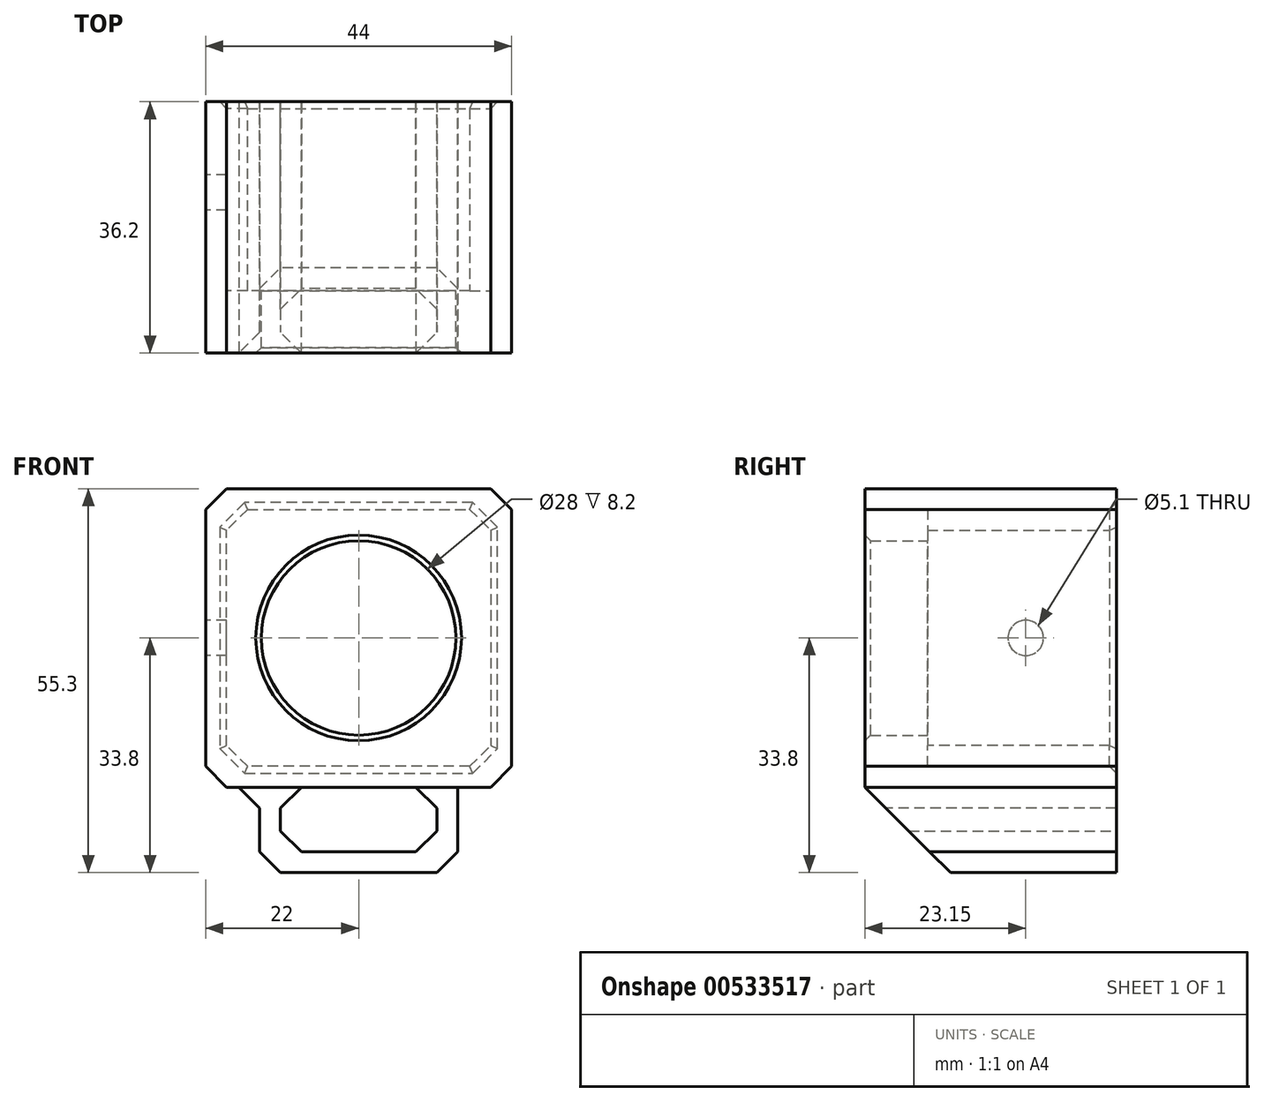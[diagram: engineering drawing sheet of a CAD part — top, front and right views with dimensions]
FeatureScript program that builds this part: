
annotation { "Feature Type Name" : "Feature", "Feature Type Description" : "" }
export const myFeature = defineFeature(function(context is Context, id is Id, definition is map)
    precondition{}
    {
        {
            var Q0;
            Q0=qCreatedBy(makeId("Front.planeOp"),FACE);
            var sketch = newSketch(context, id + "F0", { "sketchPlane" : qUnion([Q0])});
            skLineSegment(sketch, "E0.bottom", {"start": v(19, 18.5) * mm, "end": v(-19, 18.5) * mm});
            skLineSegment(sketch, "E0.top", {"start": v(19, -18.5) * mm, "end": v(-19, -18.5) * mm});
            skLineSegment(sketch, "E0.left", {"start": v(19, 18.5) * mm, "end": v(19, -18.5) * mm});
            skLineSegment(sketch, "E0.right", {"start": v(-19, 18.5) * mm, "end": v(-19, -18.5) * mm});
            skPoint(sketch, "E0.middle", {"position": v(0, 0) * mm});
            skLineSegment(sketch, "E1.0", {"start": v(22, 21.5) * mm, "end": v(-22, 21.5) * mm});
            skLineSegment(sketch, "E1.1", {"start": v(22, 21.5) * mm, "end": v(22, -21.5) * mm});
            skLineSegment(sketch, "E1.2", {"start": v(22, -21.5) * mm, "end": v(-22, -21.5) * mm});
            skLineSegment(sketch, "E1.3", {"start": v(-22, 21.5) * mm, "end": v(-22, -21.5) * mm});
            skSolve(sketch);
        }
        {
            var Q0;
            Q0 = qSketchRegion(id + "F0", true);
            extrude(context, id + "F1", {"entities" : qUnion([Q0]), "depth" : 27.2 * mm, "offsetDistance" : 25 * mm});
        }
        {
            var Q0;
            Q0=makeQuery(id+"F1.opExtrude","CAP_FACE",FACE,{"disambiguationData":[OSD([sQuery(id+"F0.wireOp",EDGE,"E0.bottom"),sQuery(id+"F0.wireOp",EDGE,"E0.top"),sQuery(id+"F0.wireOp",EDGE,"E0.left"),sQuery(id+"F0.wireOp",EDGE,"E0.right"),sQuery(id+"F0.wireOp",EDGE,"E1.0"),sQuery(id+"F0.wireOp",EDGE,"E1.1"),sQuery(id+"F0.wireOp",EDGE,"E1.2"),sQuery(id+"F0.wireOp",EDGE,"E1.3")])],"isStart":false});
            var sketch = newSketch(context, id + "F2", { "sketchPlane" : qUnion([Q0])});
            skLineSegment(sketch, "E2.0", {"start": v(22, 21.5) * mm, "end": v(-22, 21.5) * mm});
            skLineSegment(sketch, "E3.0", {"start": v(-22, 21.5) * mm, "end": v(-22, -21.5) * mm});
            skLineSegment(sketch, "E4.0", {"start": v(22, -21.5) * mm, "end": v(-22, -21.5) * mm});
            skLineSegment(sketch, "E5.0", {"start": v(22, 21.5) * mm, "end": v(22, -21.5) * mm});
            skCircle(sketch, "E6", {"center": v(0, 0) * mm, "radius": 14 * mm});
            skSolve(sketch);
        }
        {
            var Q0;
            Q0 = qSketchRegion(id + "F2", true);
            extrude(context, id + "F3", {"entities" : qUnion([Q0]), "operationType" : NewBodyOperationType.ADD, "depth" : 9 * mm, "offsetDistance" : 25 * mm});
        }
        {
            var Q0;
            Q0=makeQuery(id+"F3.boolean.opBoolean","MERGE",EDGE,{"derivedFrom":[makeQuery(id+"F1.opExtrude","SWEPT_EDGE",EDGE,{"disambiguationData":[OSD([sQuery(id+"F0.wireOp",EDGE,"E1.0"),sQuery(id+"F0.wireOp",EDGE,"E1.1")])]}),makeQuery(id+"F3.opExtrude","SWEPT_EDGE",EDGE,{"disambiguationData":[OSD([sQuery(id+"F2.wireOp",EDGE,"E2.0"),sQuery(id+"F2.wireOp",EDGE,"E5.0")])]})]});
            var Q1;
            Q1=makeQuery(id+"F3.boolean.opBoolean","MERGE",EDGE,{"derivedFrom":[makeQuery(id+"F1.opExtrude","SWEPT_EDGE",EDGE,{"disambiguationData":[OSD([sQuery(id+"F0.wireOp",EDGE,"E1.1"),sQuery(id+"F0.wireOp",EDGE,"E1.2")])]}),makeQuery(id+"F3.opExtrude","SWEPT_EDGE",EDGE,{"disambiguationData":[OSD([sQuery(id+"F2.wireOp",EDGE,"E4.0"),sQuery(id+"F2.wireOp",EDGE,"E5.0")])]})]});
            var Q2;
            Q2=makeQuery(id+"F3.boolean.opBoolean","MERGE",EDGE,{"derivedFrom":[makeQuery(id+"F1.opExtrude","SWEPT_EDGE",EDGE,{"disambiguationData":[OSD([sQuery(id+"F0.wireOp",EDGE,"E1.2"),sQuery(id+"F0.wireOp",EDGE,"E1.3")])]}),makeQuery(id+"F3.opExtrude","SWEPT_EDGE",EDGE,{"disambiguationData":[OSD([sQuery(id+"F2.wireOp",EDGE,"E3.0"),sQuery(id+"F2.wireOp",EDGE,"E4.0")])]})]});
            var Q3;
            Q3=makeQuery(id+"F3.boolean.opBoolean","MERGE",EDGE,{"derivedFrom":[makeQuery(id+"F1.opExtrude","SWEPT_EDGE",EDGE,{"disambiguationData":[OSD([sQuery(id+"F0.wireOp",EDGE,"E1.0"),sQuery(id+"F0.wireOp",EDGE,"E1.3")])]}),makeQuery(id+"F3.opExtrude","SWEPT_EDGE",EDGE,{"disambiguationData":[OSD([sQuery(id+"F2.wireOp",EDGE,"E2.0"),sQuery(id+"F2.wireOp",EDGE,"E3.0")])]})]});
            var Q4;
            Q4=makeQuery(id+"F1.opExtrude","SWEPT_EDGE",EDGE,{"disambiguationData":[OSD([sQuery(id+"F0.wireOp",EDGE,"E0.bottom"),sQuery(id+"F0.wireOp",EDGE,"E0.right")])]});
            var Q5;
            Q5=makeQuery(id+"F1.opExtrude","SWEPT_EDGE",EDGE,{"disambiguationData":[OSD([sQuery(id+"F0.wireOp",EDGE,"E0.top"),sQuery(id+"F0.wireOp",EDGE,"E0.right")])]});
            var Q6;
            Q6=makeQuery(id+"F1.opExtrude","SWEPT_EDGE",EDGE,{"disambiguationData":[OSD([sQuery(id+"F0.wireOp",EDGE,"E0.top"),sQuery(id+"F0.wireOp",EDGE,"E0.left")])]});
            var Q7;
            Q7=makeQuery(id+"F1.opExtrude","SWEPT_EDGE",EDGE,{"disambiguationData":[OSD([sQuery(id+"F0.wireOp",EDGE,"E0.bottom"),sQuery(id+"F0.wireOp",EDGE,"E0.left")])]});
            chamfer(context, id + "F4", {"entities" : qUnion([Q0, Q1, Q2, Q3, Q4, Q5, Q6, Q7]), "width" : 3 * mm, "tangentPropagation" : true});
        }
        {
            var Q0;
            Q0=makeQuery(id+"F3.opExtrude","CAP_FACE",FACE,{"disambiguationData":[OSD([sQuery(id+"F2.wireOp",EDGE,"E2.0"),sQuery(id+"F2.wireOp",EDGE,"E3.0"),sQuery(id+"F2.wireOp",EDGE,"E4.0"),sQuery(id+"F2.wireOp",EDGE,"E5.0"),sQuery(id+"F2.wireOp",EDGE,"E6")])],"isStart":false});
            var sketch = newSketch(context, id + "F5", { "sketchPlane" : qUnion([Q0])});
            skLineSegment(sketch, "E7.0", {"start": v(16, -18.5) * mm, "end": v(-16, -18.5) * mm, "construction": true});
            skLineSegment(sketch, "E8.0", {"start": v(14.25, -33.8) * mm, "end": v(-14.25, -33.8) * mm});
            skPoint(sketch, "E9", {"position": v(0, -33.8) * mm});
            skPoint(sketch, "E10", {"position": v(0, -18.5) * mm});
            skLineSegment(sketch, "E11", {"start": v(-14.25, -33.8) * mm, "end": v(-14.25, -21.5) * mm});
            skLineSegment(sketch, "E12", {"start": v(14.25, -33.8) * mm, "end": v(14.25, -21.5) * mm});
            skLineSegment(sketch, "E13", {"start": v(14.25, -21.5) * mm, "end": v(11.25, -21.5) * mm});
            skLineSegment(sketch, "E14.0", {"start": v(-11.25, -30.8) * mm, "end": v(-11.25, -21.5) * mm});
            skLineSegment(sketch, "E14.1", {"start": v(11.25, -30.8) * mm, "end": v(-11.25, -30.8) * mm});
            skLineSegment(sketch, "E14.2", {"start": v(11.25, -30.8) * mm, "end": v(11.25, -21.5) * mm});
            skLineSegment(sketch, "E15.trimOffspring", {"start": v(-11.25, -21.5) * mm, "end": v(-14.25, -21.5) * mm});
            skSolve(sketch);
        }
        {
            var Q0;
            Q0 = qSketchRegion(id + "F5", true);
            var Q1;
            Q1=qCreatedBy(makeId("Front.planeOp"),FACE);
            extrude(context, id + "F6", {"entities" : qUnion([Q0]), "operationType" : NewBodyOperationType.ADD, "endBound" : BoundingType.UP_TO_SURFACE, "oppositeDirection" : true, "depth" : 25 * mm, "endBoundEntityFace" : qUnion([Q1]), "offsetDistance" : 25 * mm});
        }
        {
            var Q0;
            Q0=makeQuery(id+"F6.opExtrude","SWEPT_EDGE",EDGE,{"disambiguationData":[OSD([sQuery(id+"F5.wireOp",EDGE,"E8.0"),sQuery(id+"F5.wireOp",EDGE,"E11")])]});
            var Q1;
            Q1=makeQuery(id+"F6.opExtrude","SWEPT_EDGE",EDGE,{"disambiguationData":[OSD([sQuery(id+"F2.wireOp",EDGE,"E4.0"),sQuery(id+"F5.wireOp",EDGE,"E11"),sQuery(id+"F5.wireOp",EDGE,"E15.trimOffspring")])]});
            var Q2;
            Q2=makeQuery(id+"F6.opExtrude","SWEPT_EDGE",EDGE,{"disambiguationData":[OSD([sQuery(id+"F5.wireOp",EDGE,"E14.0"),sQuery(id+"F5.wireOp",EDGE,"E14.1")])]});
            var Q3;
            Q3=makeQuery(id+"F6.opExtrude","SWEPT_EDGE",EDGE,{"disambiguationData":[OSD([sQuery(id+"F5.wireOp",EDGE,"E14.1"),sQuery(id+"F5.wireOp",EDGE,"E14.2")])]});
            var Q4;
            Q4=makeQuery(id+"F6.opExtrude","SWEPT_EDGE",EDGE,{"disambiguationData":[OSD([sQuery(id+"F2.wireOp",EDGE,"E4.0"),sQuery(id+"F5.wireOp",EDGE,"E13"),sQuery(id+"F5.wireOp",EDGE,"E14.2")])]});
            var Q5;
            Q5=makeQuery(id+"F6.opExtrude","SWEPT_EDGE",EDGE,{"disambiguationData":[OSD([sQuery(id+"F5.wireOp",EDGE,"E8.0"),sQuery(id+"F5.wireOp",EDGE,"E12")])]});
            var Q6;
            Q6=makeQuery(id+"F6.opExtrude","SWEPT_EDGE",EDGE,{"disambiguationData":[OSD([sQuery(id+"F2.wireOp",EDGE,"E4.0"),sQuery(id+"F5.wireOp",EDGE,"E12"),sQuery(id+"F5.wireOp",EDGE,"E13")])]});
            var Q7;
            Q7=makeQuery(id+"F6.opExtrude","SWEPT_EDGE",EDGE,{"disambiguationData":[OSD([sQuery(id+"F2.wireOp",EDGE,"E4.0"),sQuery(id+"F5.wireOp",EDGE,"E14.0"),sQuery(id+"F5.wireOp",EDGE,"E15.trimOffspring")])]});
            chamfer(context, id + "F7", {"entities" : qUnion([Q0, Q1, Q2, Q3, Q4, Q5, Q6, Q7]), "width" : 3 * mm, "tangentPropagation" : true});
        }
        {
            var Q0;
            Q0=makeQuery(id+"F6.opExtrude","CAP_EDGE",EDGE,{"disambiguationData":[OSD([sQuery(id+"F5.wireOp",EDGE,"E8.0")])],"isStart":true});
            chamfer(context, id + "F8", {"entities" : qUnion([Q0]), "width" : 12.3 * mm, "tangentPropagation" : true});
        }
        {
            var Q0;
            Q0=makeQuery(id+"F3.boolean.opBoolean","MERGE",FACE,{"derivedFrom":[makeQuery(id+"F1.opExtrude","SWEPT_FACE",FACE,{"disambiguationData":[OSD([sQuery(id+"F0.wireOp",EDGE,"E1.3")])]}),makeQuery(id+"F3.opExtrude","SWEPT_FACE",FACE,{"disambiguationData":[OSD([sQuery(id+"F2.wireOp",EDGE,"E3.0")])]})]});
            var sketch = newSketch(context, id + "F9", { "sketchPlane" : qUnion([Q0])});
            skCircle(sketch, "E16", {"center": v(13.05, 0) * mm, "radius": 2.55 * mm});
            skSolve(sketch);
        }
        {
            var Q0;
            Q0 = qSketchRegion(id + "F9", true);
            var Q1;
            Q1=makeQuery(id+"F1.opExtrude","SWEPT_FACE",FACE,{"disambiguationData":[OSD([sQuery(id+"F0.wireOp",EDGE,"E0.right")])]});
            extrude(context, id + "F10", {"entities" : qUnion([Q0]), "operationType" : NewBodyOperationType.REMOVE, "endBound" : BoundingType.UP_TO_SURFACE, "oppositeDirection" : true, "depth" : 25 * mm, "endBoundEntityFace" : qUnion([Q1]), "offsetDistance" : 25 * mm});
        }
        {
            var Q0;
            Q0=makeQuery(id+"F3.opExtrude","CAP_EDGE",EDGE,{"disambiguationData":[OSD([sQuery(id+"F2.wireOp",EDGE,"E6")])],"isStart":false});
            chamfer(context, id + "F11", {"entities" : qUnion([Q0]), "width" : .8 * mm, "tangentPropagation" : true});
        }
        {
            var Q0;
            Q0=makeQuery(id+"F1.opExtrude","CAP_EDGE",EDGE,{"disambiguationData":[OSD([sQuery(id+"F0.wireOp",EDGE,"E0.bottom")])],"isStart":true});
            var Q1;
            {var subQ0=sQuery(id+"F0.wireOp",EDGE,"E0.left");var subQ1=sQuery(id+"F0.wireOp",EDGE,"E0.bottom");Q1=makeQuery(id+"F4.opChamfer","BLEND_EDGE",EDGE,{"blendedFrom":[makeQuery(id+"F1.opExtrude","SWEPT_EDGE",EDGE,{"disambiguationData":[OSD([subQ1,subQ0])]}),makeQuery(id+"F1.opExtrude","CAP_FACE",FACE,{"disambiguationData":[OSD([subQ1,sQuery(id+"F0.wireOp",EDGE,"E0.top"),subQ0,sQuery(id+"F0.wireOp",EDGE,"E0.right"),sQuery(id+"F0.wireOp",EDGE,"E1.0"),sQuery(id+"F0.wireOp",EDGE,"E1.1"),sQuery(id+"F0.wireOp",EDGE,"E1.2"),sQuery(id+"F0.wireOp",EDGE,"E1.3")])],"isStart":true})],"blendedInto":[makeQuery(id+"F1.opExtrude","CAP_FACE",FACE,{"disambiguationData":[OSD([subQ1,sQuery(id+"F0.wireOp",EDGE,"E0.top"),subQ0,sQuery(id+"F0.wireOp",EDGE,"E0.right"),sQuery(id+"F0.wireOp",EDGE,"E1.0"),sQuery(id+"F0.wireOp",EDGE,"E1.1"),sQuery(id+"F0.wireOp",EDGE,"E1.2"),sQuery(id+"F0.wireOp",EDGE,"E1.3")])],"isStart":true})]});}
            var Q2;
            Q2=makeQuery(id+"F1.opExtrude","CAP_EDGE",EDGE,{"disambiguationData":[OSD([sQuery(id+"F0.wireOp",EDGE,"E0.left")])],"isStart":true});
            var Q3;
            {var subQ0=sQuery(id+"F0.wireOp",EDGE,"E0.left");var subQ1=sQuery(id+"F0.wireOp",EDGE,"E0.top");Q3=makeQuery(id+"F4.opChamfer","BLEND_EDGE",EDGE,{"blendedFrom":[makeQuery(id+"F1.opExtrude","SWEPT_EDGE",EDGE,{"disambiguationData":[OSD([subQ1,subQ0])]}),makeQuery(id+"F1.opExtrude","CAP_FACE",FACE,{"disambiguationData":[OSD([sQuery(id+"F0.wireOp",EDGE,"E0.bottom"),subQ1,subQ0,sQuery(id+"F0.wireOp",EDGE,"E0.right"),sQuery(id+"F0.wireOp",EDGE,"E1.0"),sQuery(id+"F0.wireOp",EDGE,"E1.1"),sQuery(id+"F0.wireOp",EDGE,"E1.2"),sQuery(id+"F0.wireOp",EDGE,"E1.3")])],"isStart":true})],"blendedInto":[makeQuery(id+"F1.opExtrude","CAP_FACE",FACE,{"disambiguationData":[OSD([sQuery(id+"F0.wireOp",EDGE,"E0.bottom"),subQ1,subQ0,sQuery(id+"F0.wireOp",EDGE,"E0.right"),sQuery(id+"F0.wireOp",EDGE,"E1.0"),sQuery(id+"F0.wireOp",EDGE,"E1.1"),sQuery(id+"F0.wireOp",EDGE,"E1.2"),sQuery(id+"F0.wireOp",EDGE,"E1.3")])],"isStart":true})]});}
            var Q4;
            Q4=makeQuery(id+"F1.opExtrude","CAP_EDGE",EDGE,{"disambiguationData":[OSD([sQuery(id+"F0.wireOp",EDGE,"E0.top")])],"isStart":true});
            var Q5;
            {var subQ0=sQuery(id+"F0.wireOp",EDGE,"E0.right");var subQ1=sQuery(id+"F0.wireOp",EDGE,"E0.top");Q5=makeQuery(id+"F4.opChamfer","BLEND_EDGE",EDGE,{"blendedFrom":[makeQuery(id+"F1.opExtrude","SWEPT_EDGE",EDGE,{"disambiguationData":[OSD([subQ1,subQ0])]}),makeQuery(id+"F1.opExtrude","CAP_FACE",FACE,{"disambiguationData":[OSD([sQuery(id+"F0.wireOp",EDGE,"E0.bottom"),subQ1,sQuery(id+"F0.wireOp",EDGE,"E0.left"),subQ0,sQuery(id+"F0.wireOp",EDGE,"E1.0"),sQuery(id+"F0.wireOp",EDGE,"E1.1"),sQuery(id+"F0.wireOp",EDGE,"E1.2"),sQuery(id+"F0.wireOp",EDGE,"E1.3")])],"isStart":true})],"blendedInto":[makeQuery(id+"F1.opExtrude","CAP_FACE",FACE,{"disambiguationData":[OSD([sQuery(id+"F0.wireOp",EDGE,"E0.bottom"),subQ1,sQuery(id+"F0.wireOp",EDGE,"E0.left"),subQ0,sQuery(id+"F0.wireOp",EDGE,"E1.0"),sQuery(id+"F0.wireOp",EDGE,"E1.1"),sQuery(id+"F0.wireOp",EDGE,"E1.2"),sQuery(id+"F0.wireOp",EDGE,"E1.3")])],"isStart":true})]});}
            var Q6;
            Q6=makeQuery(id+"F1.opExtrude","CAP_EDGE",EDGE,{"disambiguationData":[OSD([sQuery(id+"F0.wireOp",EDGE,"E0.right")])],"isStart":true});
            var Q7;
            {var subQ0=sQuery(id+"F0.wireOp",EDGE,"E0.right");var subQ1=sQuery(id+"F0.wireOp",EDGE,"E0.bottom");Q7=makeQuery(id+"F4.opChamfer","BLEND_EDGE",EDGE,{"blendedFrom":[makeQuery(id+"F1.opExtrude","SWEPT_EDGE",EDGE,{"disambiguationData":[OSD([subQ1,subQ0])]}),makeQuery(id+"F1.opExtrude","CAP_FACE",FACE,{"disambiguationData":[OSD([subQ1,sQuery(id+"F0.wireOp",EDGE,"E0.top"),sQuery(id+"F0.wireOp",EDGE,"E0.left"),subQ0,sQuery(id+"F0.wireOp",EDGE,"E1.0"),sQuery(id+"F0.wireOp",EDGE,"E1.1"),sQuery(id+"F0.wireOp",EDGE,"E1.2"),sQuery(id+"F0.wireOp",EDGE,"E1.3")])],"isStart":true})],"blendedInto":[makeQuery(id+"F1.opExtrude","CAP_FACE",FACE,{"disambiguationData":[OSD([subQ1,sQuery(id+"F0.wireOp",EDGE,"E0.top"),sQuery(id+"F0.wireOp",EDGE,"E0.left"),subQ0,sQuery(id+"F0.wireOp",EDGE,"E1.0"),sQuery(id+"F0.wireOp",EDGE,"E1.1"),sQuery(id+"F0.wireOp",EDGE,"E1.2"),sQuery(id+"F0.wireOp",EDGE,"E1.3")])],"isStart":true})]});}
            chamfer(context, id + "F12", {"entities" : qUnion([Q0, Q1, Q2, Q3, Q4, Q5, Q6, Q7]), "width" : 1 * mm, "tangentPropagation" : true});
        }
    });
